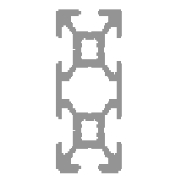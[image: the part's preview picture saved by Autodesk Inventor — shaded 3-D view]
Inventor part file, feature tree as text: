
AUTODESK INVENTOR PART (.ipt)
format: ipt  version: 2023.2 (Build 272271000, 271)  size: 621,568 bytes
history: native  units: mm
features: other x9, sketch x4, reference x2, hole x1, plane x1
ambient origin geometry x8: Origin, YZ Plane, XZ Plane, XY Plane, X Axis, Y Axis, Z Axis, Center Point
bodies: Body (feature_tree)
feature tree (17):
  other  "Driven Length"
  other  "Blocks"
  other  "Start Plane"
  other  "End Plane"
  hole  "Hole1"  [1 undecoded]
  sketch  "Sketch1"  dims[d16=-0.0mm d17=300.0mm]
  other  "20x40"
  sketch  "Sketch10"  dims[d18=0.13mm d19=0.0mm]
  plane  "Work Plane9"
  sketch  "Sketch11"  dims[d20=90.0deg]
  sketch  "Sketch12"  dims[d21=300.0mm d22=5.1mm d23=6.0mm d24=4.0mm d25=2.0mm d26=90.0deg d27=8.0mm d28=20.594885mm]
  reference  "Reference1"
  reference  "Reference2"
  other  "20x40:1"
  parser-record x1  (decoder bookkeeping rows leaked as tree rows — omitted from the tree; the rows remain in map.json)
  other  "Main Assembly.iam"
  other  "X axis motor mount:1"
note: 1 required parameter value undecoded (feature->parameter linkage not recoverable at this tier; creation-order binding heuristic only, values carry confidence <= 0.55)
note: 1 file-system path scrubbed to <path> (originals preserved in map.json)
